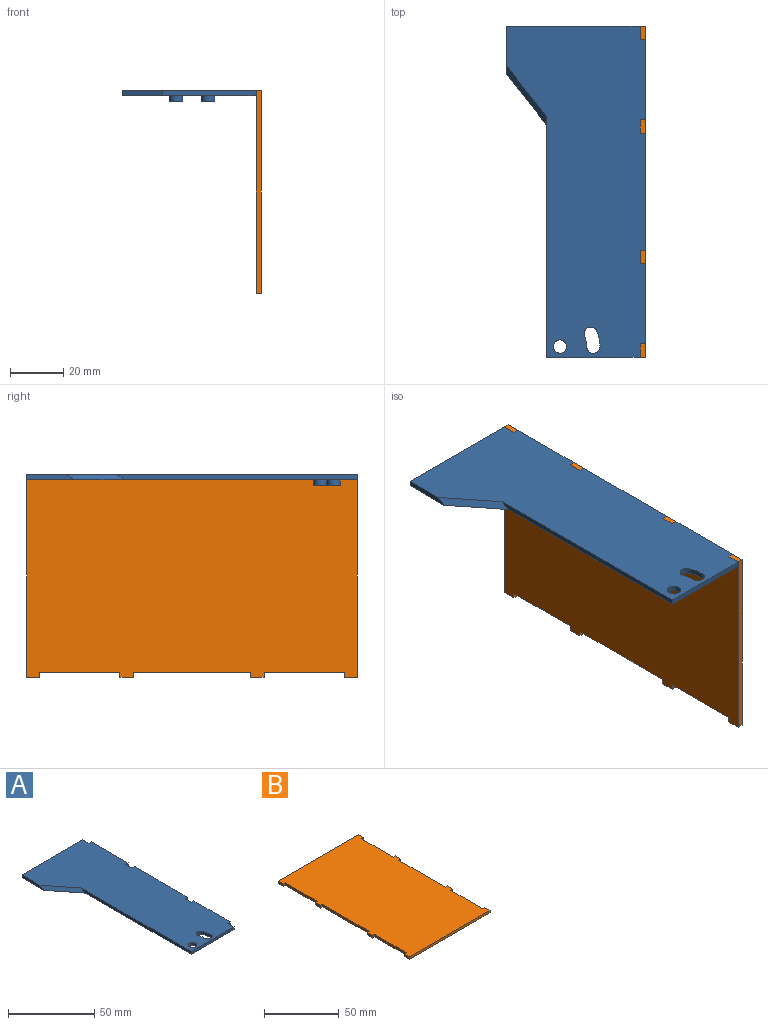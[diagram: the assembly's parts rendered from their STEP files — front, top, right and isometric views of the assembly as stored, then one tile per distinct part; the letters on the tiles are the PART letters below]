
ASSEMBLY  parts=2 mates=1
PART A: 29 faces, bbox 52x124x4 mm
  f0: plane 50x2mm, normal (0,1,0), area 100mm2, adj f4,f5,f8,f23
  f1: plane 30x2mm, normal (1,0,0), area 60mm2, adj f4,f5,f21,f27
  f2: plane 30x2mm, normal (1,0,0), area 60mm2, adj f4,f5,f22,f24
  f3: plane 44x2mm, normal (1,0,0), area 88mm2, adj f4,f5,f19,f26
  f4: plane 124x52mm, normal (0,0,1), area 4848.3mm2, adj f0,f1,f2,f3,f6,f7,f8,f13
  f5: plane 124x52mm, normal (0,0,-1), area 4857.4mm2, adj f0,f1,f2,f3,f6,f7,f8,f9
  f6: plane 90.23x2mm, normal (-1,0,0), area 177.2mm2, adj f4,f5,f7,f18
  f7: plane 35x2mm, normal (0,-1,0), area 70mm2, adj f4,f5,f6,f28
  f8: plane 18x2mm, normal (-1,0,0), area 32.8mm2, adj f0,f4,f5,f18
  f9: cylinder r=2.5mm len=5mm, axis (0,0,1), area 31.4mm2, adj f5,f10
  f10: plane 5x5mm, normal (0,0,-1), area 19.6mm2, adj f9
  f11: cylinder r=2.5mm len=5mm, axis (0,0,1), area 31.4mm2, adj f5,f12
  f12: plane 5x5mm, normal (0,0,-1), area 19.6mm2, adj f11
  f13: cylinder r=10mm len=3.83mm, axis (0,0,-1), area 7.9mm2, adj f4,f5,f14,f16
  f14: cylinder r=2.5mm len=5mm, axis (0,0,-1), area 15.7mm2, adj f4,f5,f13,f15
  f15: cylinder r=15mm len=5.74mm, axis (0,0,-1), area 11.8mm2, adj f4,f5,f14,f16
  f16: cylinder r=2.5mm len=4.81mm, axis (0,0,-1), area 15.7mm2, adj f4,f5,f13,f15
  f17: cylinder r=2.5mm len=5mm, axis (0,0,-1), area 31.4mm2, adj f4,f5
  f18: plane 22.23x15mm, normal (-0.55,-0.44,0.71), area 68.5mm2, adj f4,f5,f6,f8
  f19: plane 2x2mm, normal (0,-1,0), area 4mm2, adj f3,f4,f5,f20
  f20: plane 5x2mm, normal (1,0,0), area 10mm2, adj f4,f5,f19,f21
  f21: plane 2x2mm, normal (0,1,0), area 4mm2, adj f1,f4,f5,f20
  f22: plane 2x2mm, normal (0,1,0), area 4mm2, adj f2,f4,f5,f23
  f23: plane 5x2mm, normal (1,0,0), area 10mm2, adj f0,f4,f5,f22
  f24: plane 2x2mm, normal (0,-1,0), area 4mm2, adj f2,f4,f5,f25
  f25: plane 5x2mm, normal (1,0,0), area 10mm2, adj f4,f5,f24,f26
  f26: plane 2x2mm, normal (0,1,0), area 4mm2, adj f3,f4,f5,f25
  f27: plane 2x2mm, normal (0,-1,0), area 4mm2, adj f1,f4,f5,f28
  f28: plane 5x2mm, normal (1,0,0), area 10mm2, adj f4,f5,f7,f27
PART B: 30 faces, bbox 76x124x2 mm
  f0: plane 76x2mm, normal (0,1,0), area 152mm2, adj f1,f27,f28,f29
  f1: plane 5x2mm, normal (-1,0,0), area 10mm2, adj f0,f2,f28,f29
  f2: plane 2x2mm, normal (0,-1,0), area 4mm2, adj f1,f3,f28,f29
  f3: plane 30x2mm, normal (-1,0,0), area 60mm2, adj f2,f4,f28,f29
  f4: plane 2x2mm, normal (0,1,0), area 4mm2, adj f3,f5,f28,f29
  f5: plane 5x2mm, normal (-1,0,0), area 10mm2, adj f4,f6,f28,f29
  f6: plane 2x2mm, normal (0,-1,0), area 4mm2, adj f5,f7,f28,f29
  f7: plane 44x2mm, normal (-1,0,0), area 88mm2, adj f6,f8,f28,f29
  f8: plane 2x2mm, normal (0,1,0), area 4mm2, adj f7,f9,f28,f29
  f9: plane 5x2mm, normal (-1,0,0), area 10mm2, adj f8,f10,f28,f29
  f10: plane 2x2mm, normal (0,-1,0), area 4mm2, adj f9,f11,f28,f29
  f11: plane 30x2mm, normal (-1,0,0), area 60mm2, adj f10,f12,f28,f29
  f12: plane 2x2mm, normal (0,1,0), area 4mm2, adj f11,f13,f28,f29
  f13: plane 5x2mm, normal (-1,0,0), area 10mm2, adj f12,f14,f28,f29
  f14: plane 76x2mm, normal (0,-1,0), area 152mm2, adj f13,f15,f28,f29
  f15: plane 5x2mm, normal (1,0,0), area 10mm2, adj f14,f16,f28,f29
  f16: plane 2x2mm, normal (0,1,0), area 4mm2, adj f15,f17,f28,f29
  f17: plane 30x2mm, normal (1,0,0), area 60mm2, adj f16,f18,f28,f29
  f18: plane 2x2mm, normal (0,-1,0), area 4mm2, adj f17,f19,f28,f29
  f19: plane 5x2mm, normal (1,0,0), area 10mm2, adj f18,f20,f28,f29
  f20: plane 2x2mm, normal (0,1,0), area 4mm2, adj f19,f21,f28,f29
  f21: plane 44x2mm, normal (1,0,0), area 88mm2, adj f20,f22,f28,f29
  f22: plane 2x2mm, normal (0,-1,0), area 4mm2, adj f21,f23,f28,f29
  f23: plane 5x2mm, normal (1,0,0), area 10mm2, adj f22,f24,f28,f29
  f24: plane 2x2mm, normal (0,1,0), area 4mm2, adj f23,f25,f28,f29
  f25: plane 30x2mm, normal (1,0,0), area 60mm2, adj f24,f26,f28,f29
  f26: plane 2x2mm, normal (0,-1,0), area 4mm2, adj f25,f27,f28,f29
  f27: plane 5x2mm, normal (1,0,0), area 10mm2, adj f0,f26,f28,f29
  f28: plane 124x76mm, normal (0,0,1), area 9008mm2, adj f0,f1,f2,f3,f4,f5,f6,f7
  f29: plane 124x76mm, normal (0,0,-1), area 9008mm2, adj f0,f1,f2,f3,f4,f5,f6,f7
PLACE A t=(-11.35,-58.2,0)mm
PLACE B rot(axis=(0,1,0),90deg) t=(18.65,-16.41,-35.18)mm
MATE fastened B.f29 <-> A.f23  axis (-1,0,0) through (18.65,54.3,2)mm
